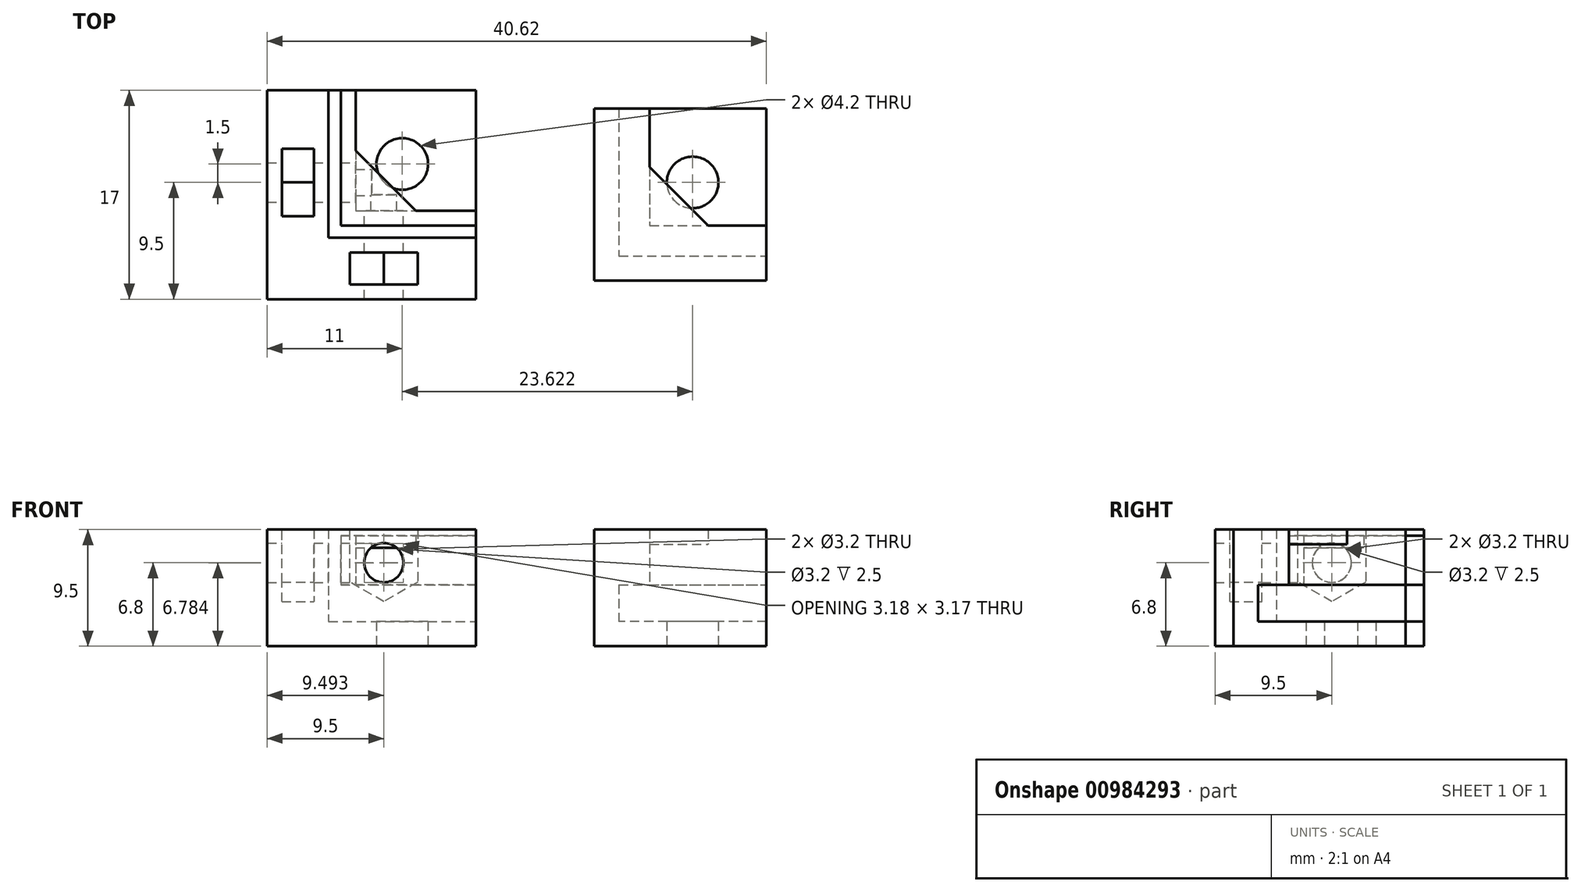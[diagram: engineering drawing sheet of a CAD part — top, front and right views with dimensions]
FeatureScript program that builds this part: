
annotation { "Feature Type Name" : "Feature", "Feature Type Description" : "" }
export const myFeature = defineFeature(function(context is Context, id is Id, definition is map)
    precondition{}
    {
        {
            var Q0;
            Q0=qCreatedBy(makeId("Top.planeOp"),FACE);
            var sketch = newSketch(context, id + "F0", { "sketchPlane" : qUnion([Q0])});
            skLineSegment(sketch, "E0.bottom", {"start": v(-8.5, 8.5) * mm, "end": v(8.5, 8.5) * mm});
            skLineSegment(sketch, "E0.top", {"start": v(-8.5, -8.5) * mm, "end": v(8.5, -8.5) * mm});
            skLineSegment(sketch, "E0.left", {"start": v(-8.5, 8.5) * mm, "end": v(-8.5, -8.5) * mm});
            skLineSegment(sketch, "E0.right", {"start": v(8.5, 8.5) * mm, "end": v(8.5, -8.5) * mm});
            skPoint(sketch, "E0.middle", {"position": v(0, 0) * mm});
            skCircle(sketch, "E1", {"center": v(2.5, 2.5) * mm, "radius": 2.1 * mm});
            skLineSegment(sketch, "E2", {"start": v(-3.5, 8.5) * mm, "end": v(-3.5, -3.5) * mm});
            skLineSegment(sketch, "E3", {"start": v(-3.5, -3.5) * mm, "end": v(8.5, -3.5) * mm});
            skLineSegment(sketch, "E4.bottom", {"start": v(-7.3, 3.9) * mm, "end": v(-4.7, 3.9) * mm});
            skLineSegment(sketch, "E4.top", {"start": v(-7.3, -1.9) * mm, "end": v(-4.7, -1.9) * mm});
            skLineSegment(sketch, "E4.left", {"start": v(-7.3, 3.9) * mm, "end": v(-7.3, -1.9) * mm});
            skLineSegment(sketch, "E4.right", {"start": v(-4.7, 3.9) * mm, "end": v(-4.7, -1.9) * mm});
            skLineSegment(sketch, "E5.bottom", {"start": v(-1.9, -4.7) * mm, "end": v(3.9, -4.7) * mm});
            skLineSegment(sketch, "E5.top", {"start": v(-1.9, -7.3) * mm, "end": v(3.9, -7.3) * mm});
            skLineSegment(sketch, "E5.left", {"start": v(-1.9, -4.7) * mm, "end": v(-1.9, -7.3) * mm});
            skLineSegment(sketch, "E5.right", {"start": v(3.9, -4.7) * mm, "end": v(3.9, -7.3) * mm});
            skSolve(sketch);
        }
        {
            var Q0;
            {var subQ1=sQuery(id+"F0.wireOp",EDGE,"E0.top");Q0=makeQuery(id+"F0.imprint","IMPRINT",FACE,{"disambiguationData":[TD([[makeQuery(id+"F0.imprint","IMPRINT",EDGE,{"derivedFrom":subQ1}),1.0]])]});}
            var Q1;
            Q1=makeQuery(id+"F0.imprint","IMPRINT",FACE,{"disambiguationData":[TD([[makeQuery(id+"F0.imprint","IMPRINT",EDGE,{"derivedFrom":sQuery(id+"F0.wireOp",EDGE,"E1")}),-1.0]])]});
            var Q2;
            Q2=makeQuery(id+"F0.imprint","IMPRINT",FACE,{"disambiguationData":[TD([[makeQuery(id+"F0.imprint","IMPRINT",EDGE,{"derivedFrom":sQuery(id+"F0.wireOp",EDGE,"E4.bottom")}),-1.0]])]});
            var Q3;
            Q3=makeQuery(id+"F0.imprint","IMPRINT",FACE,{"disambiguationData":[TD([[makeQuery(id+"F0.imprint","IMPRINT",EDGE,{"derivedFrom":sQuery(id+"F0.wireOp",EDGE,"E5.bottom")}),-1.0]])]});
            extrude(context, id + "F1", {"entities" : qUnion([Q0, Q1, Q2, Q3]), "depth" : 2 * mm, "offsetDistance" : 25 * mm});
        }
        {
            var Q0;
            {var subQ1=sQuery(id+"F0.wireOp",EDGE,"E0.top");Q0=makeQuery(id+"F0.imprint","IMPRINT",FACE,{"disambiguationData":[TD([[makeQuery(id+"F0.imprint","IMPRINT",EDGE,{"derivedFrom":subQ1}),1.0]])]});}
            var Q1;
            Q1=makeQuery(id+"F0.imprint","IMPRINT",FACE,{"disambiguationData":[TD([[makeQuery(id+"F0.imprint","IMPRINT",EDGE,{"derivedFrom":sQuery(id+"F0.wireOp",EDGE,"E5.bottom")}),-1.0]])]});
            var Q2;
            Q2=makeQuery(id+"F0.imprint","IMPRINT",FACE,{"disambiguationData":[TD([[makeQuery(id+"F0.imprint","IMPRINT",EDGE,{"derivedFrom":sQuery(id+"F0.wireOp",EDGE,"E4.bottom")}),-1.0]])]});
            extrude(context, id + "F2", {"entities" : qUnion([Q0, Q1, Q2]), "operationType" : NewBodyOperationType.ADD, "depth" : 9.5 * mm, "offsetDistance" : 25 * mm});
        }
        {
            var Q0;
            Q0=qCreatedBy(makeId("Top.planeOp"),FACE);
            var sketch = newSketch(context, id + "F3", { "sketchPlane" : qUnion([Q0])});
            skLineSegment(sketch, "E6", {"start": v(-2.5, 8.5) * mm, "end": v(-1.3, 8.5) * mm});
            skLineSegment(sketch, "E7", {"start": v(-1.3, 8.5) * mm, "end": v(-1.3, -1.3) * mm});
            skLineSegment(sketch, "E8", {"start": v(-1.3, -1.3) * mm, "end": v(8.5, -1.3) * mm});
            skLineSegment(sketch, "E9", {"start": v(8.5, -1.3) * mm, "end": v(8.5, -2.5) * mm});
            skLineSegment(sketch, "E10", {"start": v(8.5, -2.5) * mm, "end": v(-2.5, -2.5) * mm});
            skLineSegment(sketch, "E11", {"start": v(-2.5, -2.5) * mm, "end": v(-2.5, 8.5) * mm});
            skLineSegment(sketch, "E12", {"start": v(-1.3, 3.6) * mm, "end": v(3.6, -1.3) * mm});
            skSolve(sketch);
        }
        {
            var Q0;
            Q0=makeQuery(id+"F3.imprint","IMPRINT",FACE,{"disambiguationData":[TD([[makeQuery(id+"F3.imprint","IMPRINT",EDGE,{"derivedFrom":sQuery(id+"F3.wireOp",EDGE,"E6")}),-1.0]])]});
            extrude(context, id + "F4", {"entities" : qUnion([Q0]), "depth" : 8 * mm, "offsetDistance" : 25 * mm, "hasSecondDirection" : true, "secondDirectionOppositeDirection" : false, "secondDirectionDepth" : 5 * mm});
        }
        {
            var Q0;
            {var subQ3=sQuery(id+"F3.wireOp",EDGE,"E12");Q0=makeQuery(id+"F3.imprint","IMPRINT",FACE,{"disambiguationData":[TD([[makeQuery(id+"F3.imprint","IMPRINT",EDGE,{"derivedFrom":subQ3}),-1.0]])]});}
            var Q1;
            {var subQ6=sQuery(id+"F3.wireOp",EDGE,"E6");Q1=makeQuery(id+"F3.imprint","IMPRINT",FACE,{"disambiguationData":[TD([[makeQuery(id+"F3.imprint","IMPRINT",EDGE,{"derivedFrom":subQ6}),-1.0]])]});}
            extrude(context, id + "F5", {"entities" : qUnion([Q0, Q1]), "operationType" : NewBodyOperationType.ADD, "depth" : 9 * mm, "offsetDistance" : 25 * mm, "hasSecondDirection" : true, "secondDirectionOppositeDirection" : false, "secondDirectionDepth" : 8 * mm});
        }
        {
            var Q0;
            Q0=qCreatedBy(makeId("Right.planeOp"),FACE);
            var sketch = newSketch(context, id + "F6", { "sketchPlane" : qUnion([Q0])});
            skCircle(sketch, "E13", {"center": v(1, 6.8) * mm, "radius": 1.6 * mm});
            skCircle(sketch, "E14.cCircle", {"center": v(1, 6.8) * mm, "radius": 2.75 * mm, "construction": true});
            skLineSegment(sketch, "E14.0", {"start": v(3.75, 8.39) * mm, "end": v(3.75, 5.21) * mm});
            skLineSegment(sketch, "E14.1", {"start": v(3.75, 5.21) * mm, "end": v(1, 3.62) * mm});
            skLineSegment(sketch, "E14.2", {"start": v(1, 3.62) * mm, "end": v(-1.75, 5.21) * mm});
            skLineSegment(sketch, "E14.3", {"start": v(-1.75, 5.21) * mm, "end": v(-1.75, 8.39) * mm});
            skLineSegment(sketch, "E14.4", {"start": v(-1.75, 8.39) * mm, "end": v(1, 9.98) * mm});
            skLineSegment(sketch, "E14.5", {"start": v(1, 9.98) * mm, "end": v(3.75, 8.39) * mm});
            skPoint(sketch, "E14.0.midPoint", {"position": v(3.75, 6.8) * mm});
            skLineSegment(sketch, "E15", {"start": v(3.75, 8.39) * mm, "end": v(3.75, 9.98) * mm});
            skLineSegment(sketch, "E16", {"start": v(3.75, 9.98) * mm, "end": v(1, 9.98) * mm});
            skLineSegment(sketch, "E17", {"start": v(1, 9.98) * mm, "end": v(-1.75, 9.98) * mm});
            skLineSegment(sketch, "E18", {"start": v(-1.75, 9.98) * mm, "end": v(-1.75, 8.39) * mm});
            skSolve(sketch);
        }
        {
            var Q0;
            Q0=makeQuery(id+"F6.imprint","IMPRINT",FACE,{"disambiguationData":[TD([[makeQuery(id+"F6.imprint","IMPRINT",EDGE,{"derivedFrom":sQuery(id+"F6.wireOp",EDGE,"E13")}),1.0]])]});
            extrude(context, id + "F7", {"entities" : qUnion([Q0]), "operationType" : NewBodyOperationType.REMOVE, "endBound" : BoundingType.THROUGH_ALL, "oppositeDirection" : true, "depth" : 25 * mm, "offsetDistance" : 25 * mm});
        }
        {
            var Q0;
            Q0=makeQuery(id+"F6.imprint","IMPRINT",FACE,{"disambiguationData":[TD([[makeQuery(id+"F6.imprint","IMPRINT",EDGE,{"derivedFrom":sQuery(id+"F6.wireOp",EDGE,"E13")}),-1.0]])]});
            var Q1;
            Q1=makeQuery(id+"F6.imprint","IMPRINT",FACE,{"disambiguationData":[TD([[makeQuery(id+"F6.imprint","IMPRINT",EDGE,{"derivedFrom":sQuery(id+"F6.wireOp",EDGE,"E14.5")}),1.0]])]});
            var Q2;
            Q2=makeQuery(id+"F6.imprint","IMPRINT",FACE,{"disambiguationData":[TD([[makeQuery(id+"F6.imprint","IMPRINT",EDGE,{"derivedFrom":sQuery(id+"F6.wireOp",EDGE,"E13")}),1.0]])]});
            var Q3;
            Q3=makeQuery(id+"F6.imprint","IMPRINT",FACE,{"disambiguationData":[TD([[makeQuery(id+"F6.imprint","IMPRINT",EDGE,{"derivedFrom":sQuery(id+"F6.wireOp",EDGE,"E14.4")}),1.0]])]});
            extrude(context, id + "F8", {"entities" : qUnion([Q0, Q1, Q2, Q3]), "operationType" : NewBodyOperationType.REMOVE, "oppositeDirection" : true, "depth" : 7.3 * mm, "offsetDistance" : 25 * mm, "hasSecondDirection" : true, "secondDirectionOppositeDirection" : true, "secondDirectionDepth" : 4.7 * mm});
        }
        {
            var Q0;
            Q0=qCreatedBy(makeId("Front.planeOp"),FACE);
            var sketch = newSketch(context, id + "F9", { "sketchPlane" : qUnion([Q0])});
            skCircle(sketch, "E19", {"center": v(1, 6.8) * mm, "radius": 1.6 * mm});
            skCircle(sketch, "E20.cCircle", {"center": v(1, 6.8) * mm, "radius": 2.75 * mm, "construction": true});
            skLineSegment(sketch, "E20.0", {"start": v(-1.75, 5.21) * mm, "end": v(-1.75, 8.39) * mm});
            skLineSegment(sketch, "E20.1", {"start": v(-1.75, 8.39) * mm, "end": v(1, 9.98) * mm});
            skLineSegment(sketch, "E20.2", {"start": v(1, 9.98) * mm, "end": v(3.75, 8.39) * mm});
            skLineSegment(sketch, "E20.3", {"start": v(3.75, 8.39) * mm, "end": v(3.75, 5.21) * mm});
            skLineSegment(sketch, "E20.4", {"start": v(3.75, 5.21) * mm, "end": v(1, 3.62) * mm});
            skLineSegment(sketch, "E20.5", {"start": v(1, 3.62) * mm, "end": v(-1.75, 5.21) * mm});
            skPoint(sketch, "E20.0.midPoint", {"position": v(-1.75, 6.8) * mm});
            skLineSegment(sketch, "E21", {"start": v(-1.75, 8.39) * mm, "end": v(-1.75, 9.98) * mm});
            skLineSegment(sketch, "E22", {"start": v(-1.75, 9.98) * mm, "end": v(3.75, 9.98) * mm});
            skLineSegment(sketch, "E23", {"start": v(3.75, 9.98) * mm, "end": v(3.75, 8.39) * mm});
            skSolve(sketch);
        }
        {
            var Q0;
            Q0=makeQuery(id+"F9.imprint","IMPRINT",FACE,{"disambiguationData":[TD([[makeQuery(id+"F9.imprint","IMPRINT",EDGE,{"derivedFrom":sQuery(id+"F9.wireOp",EDGE,"E19")}),1.0]])]});
            extrude(context, id + "F10", {"entities" : qUnion([Q0]), "operationType" : NewBodyOperationType.REMOVE, "endBound" : BoundingType.THROUGH_ALL, "depth" : 25 * mm, "offsetDistance" : 25 * mm});
        }
        {
            var Q0;
            Q0 = qSketchRegion(id + "F9", true);
            var Q1;
            Q1=makeQuery(id+"F9.imprint","IMPRINT",FACE,{"disambiguationData":[TD([[makeQuery(id+"F9.imprint","IMPRINT",EDGE,{"derivedFrom":sQuery(id+"F9.wireOp",EDGE,"E19")}),1.0]])]});
            extrude(context, id + "F11", {"entities" : qUnion([Q0, Q1]), "operationType" : NewBodyOperationType.REMOVE, "depth" : 7.3 * mm, "offsetDistance" : 25 * mm, "hasSecondDirection" : true, "secondDirectionOppositeDirection" : false, "secondDirectionDepth" : 4.7 * mm});
        }
        {
            var Q0;
            Q0=qCreatedBy(makeId("Top.planeOp"),FACE);
            var sketch = newSketch(context, id + "F12", { "sketchPlane" : qUnion([Q0])});
            skLineSegment(sketch, "E24.bottom", {"start": v(18.12, 7) * mm, "end": v(32.12, 7) * mm});
            skLineSegment(sketch, "E24.top", {"start": v(18.12, -7) * mm, "end": v(32.12, -7) * mm});
            skLineSegment(sketch, "E24.left", {"start": v(18.12, 7) * mm, "end": v(18.12, -7) * mm});
            skLineSegment(sketch, "E24.right", {"start": v(32.12, 7) * mm, "end": v(32.12, -7) * mm});
            skCircle(sketch, "E25", {"center": v(26.12, 1) * mm, "radius": 2.1 * mm});
            skLineSegment(sketch, "E26", {"start": v(20.12, 7) * mm, "end": v(20.12, -5) * mm});
            skLineSegment(sketch, "E27", {"start": v(20.12, -5) * mm, "end": v(32.12, -5) * mm});
            skLineSegment(sketch, "E28", {"start": v(22.62, 7) * mm, "end": v(22.62, -2.5) * mm});
            skLineSegment(sketch, "E29", {"start": v(22.62, -2.5) * mm, "end": v(32.12, -2.5) * mm});
            skLineSegment(sketch, "E30", {"start": v(22.62, 2.25) * mm, "end": v(27.37, -2.5) * mm});
            skSolve(sketch);
        }
        {
            var Q0;
            Q0=makeQuery(id+"F12.imprint","IMPRINT",FACE,{"disambiguationData":[TD([[makeQuery(id+"F12.imprint","IMPRINT",EDGE,{"derivedFrom":sQuery(id+"F12.wireOp",EDGE,"E25")}),-1.0]])]});
            var Q1;
            {var subQ1=sQuery(id+"F12.wireOp",EDGE,"E24.top");Q1=makeQuery(id+"F12.imprint","IMPRINT",FACE,{"disambiguationData":[TD([[makeQuery(id+"F12.imprint","IMPRINT",EDGE,{"derivedFrom":subQ1}),1.0]])]});}
            var Q2;
            {var subQ0=sQuery(id+"F12.wireOp",EDGE,"E26");Q2=makeQuery(id+"F12.imprint","IMPRINT",FACE,{"disambiguationData":[TD([[makeQuery(id+"F12.imprint","IMPRINT",EDGE,{"derivedFrom":subQ0}),1.0]])]});}
            var Q3;
            {var subQ4=sQuery(id+"F12.wireOp",EDGE,"E24.right");var subQ5=sQuery(id+"F12.wireOp",EDGE,"E24.bottom");var subQ6=makeQuery(id+"F12.imprint","INTERSECT",VERTEX,{"derivedFrom":[subQ5,subQ4]});Q3=makeQuery(id+"F12.imprint","IMPRINT",FACE,{"disambiguationData":[TD([[makeQuery(id+"F12.imprint","IMPRINT",EDGE,{"disambiguationData":[TD([[subQ6,1.0]])],"derivedFrom":subQ5}),-1.0]])]});}
            extrude(context, id + "F13", {"entities" : qUnion([Q0, Q1, Q2, Q3]), "depth" : 2 * mm, "offsetDistance" : 25 * mm});
        }
        {
            var Q0;
            {var subQ1=sQuery(id+"F12.wireOp",EDGE,"E24.top");Q0=makeQuery(id+"F12.imprint","IMPRINT",FACE,{"disambiguationData":[TD([[makeQuery(id+"F12.imprint","IMPRINT",EDGE,{"derivedFrom":subQ1}),1.0]])]});}
            extrude(context, id + "F14", {"entities" : qUnion([Q0]), "operationType" : NewBodyOperationType.ADD, "depth" : 9.5 * mm, "offsetDistance" : 25 * mm});
        }
        {
            var Q0;
            {var subQ0=sQuery(id+"F12.wireOp",EDGE,"E26");Q0=makeQuery(id+"F12.imprint","IMPRINT",FACE,{"disambiguationData":[TD([[makeQuery(id+"F12.imprint","IMPRINT",EDGE,{"derivedFrom":subQ0}),1.0]])]});}
            extrude(context, id + "F15", {"entities" : qUnion([Q0]), "operationType" : NewBodyOperationType.ADD, "depth" : 9.5 * mm, "offsetDistance" : 25 * mm, "hasSecondDirection" : true, "secondDirectionOppositeDirection" : false, "secondDirectionDepth" : 5 * mm});
        }
        {
            var Q0;
            {var subQ0=sQuery(id+"F12.wireOp",EDGE,"E30");var subQ3=sQuery(id+"F12.wireOp",EDGE,"E25");var subQ4=makeQuery(id+"F12.imprint","INTERSECT",VERTEX,{"disambiguationData":[OD(0.0)],"derivedFrom":[subQ3,subQ0]});Q0=makeQuery(id+"F12.imprint","IMPRINT",FACE,{"disambiguationData":[TD([[makeQuery(id+"F12.imprint","IMPRINT",EDGE,{"disambiguationData":[TD([[subQ4,-1.0]])],"derivedFrom":subQ3}),-1.0]])]});}
            var Q1;
            {var subQ0=sQuery(id+"F12.wireOp",EDGE,"E30");var subQ1=sQuery(id+"F12.wireOp",EDGE,"E25");var subQ2=makeQuery(id+"F12.imprint","INTERSECT",VERTEX,{"disambiguationData":[OD(0.0)],"derivedFrom":[subQ1,subQ0]});Q1=makeQuery(id+"F12.imprint","IMPRINT",FACE,{"disambiguationData":[TD([[makeQuery(id+"F12.imprint","IMPRINT",EDGE,{"disambiguationData":[TD([[subQ2,-1.0]])],"derivedFrom":subQ1}),1.0]])]});}
            extrude(context, id + "F16", {"entities" : qUnion([Q0, Q1]), "operationType" : NewBodyOperationType.ADD, "depth" : 9.5 * mm, "offsetDistance" : 25 * mm, "hasSecondDirection" : true, "secondDirectionOppositeDirection" : false, "secondDirectionDepth" : 8.3 * mm});
        }
    });
